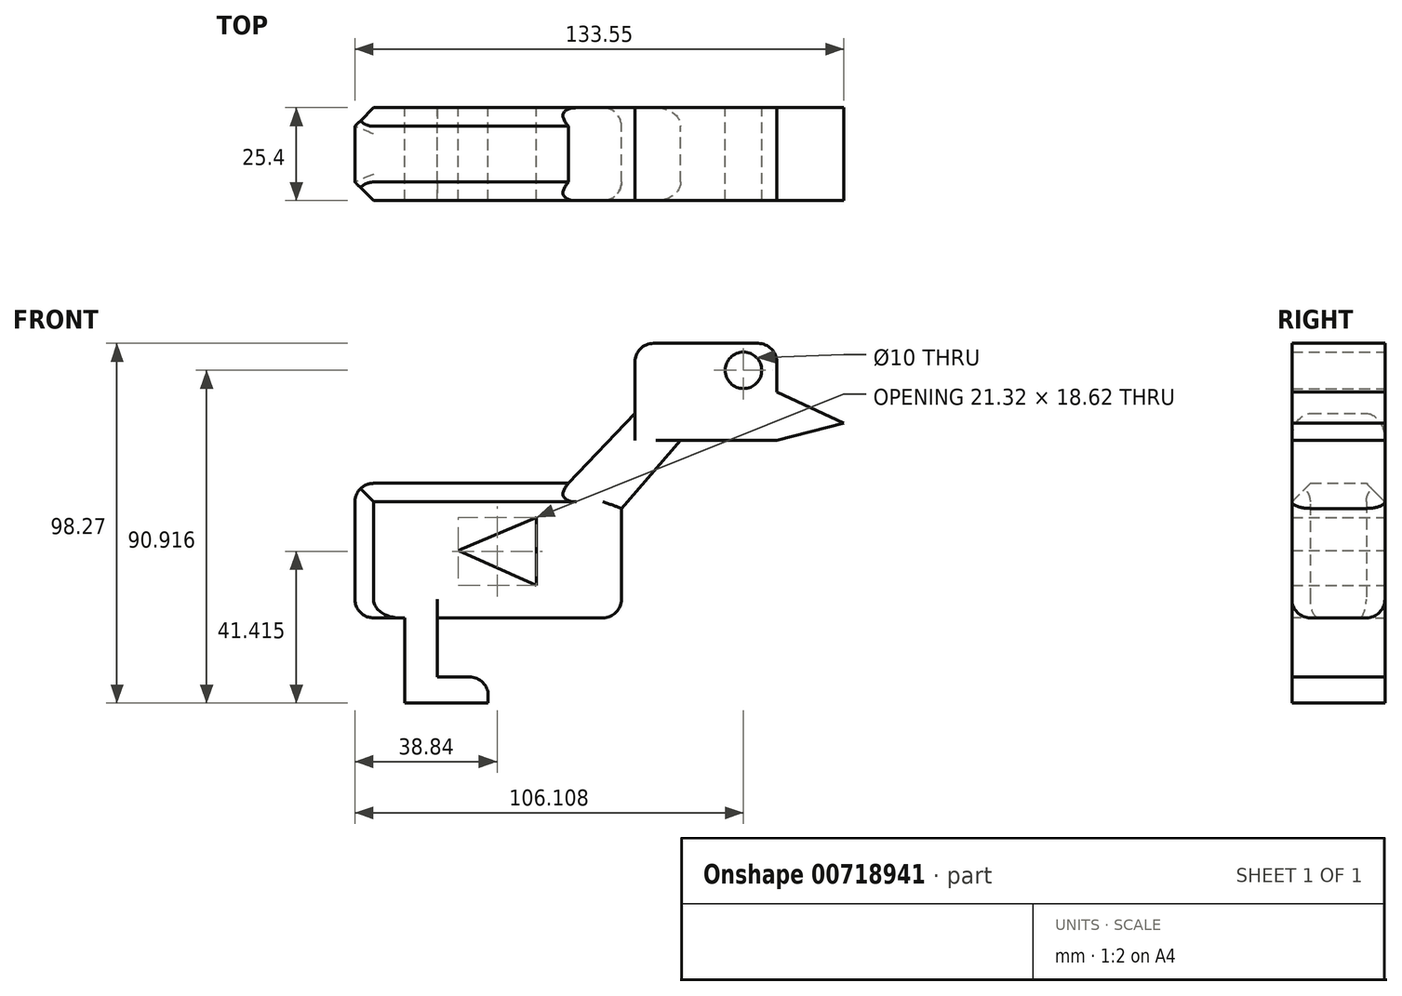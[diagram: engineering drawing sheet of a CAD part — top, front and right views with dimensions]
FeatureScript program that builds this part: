
annotation { "Feature Type Name" : "Feature", "Feature Type Description" : "" }
export const myFeature = defineFeature(function(context is Context, id is Id, definition is map)
    precondition{}
    {
        {
            var Q0;
            Q0=qCreatedBy(makeId("Front.planeOp"),FACE);
            var sketch = newSketch(context, id + "F0", { "sketchPlane" : qUnion([Q0])});
            skLineSegment(sketch, "E0.bottom", {"start": v(36.4, -18.38) * mm, "end": v(-13.9, -18.38) * mm});
            skLineSegment(sketch, "E0.top", {"start": v(36.4, 18.38) * mm, "end": v(-36.4, 18.38) * mm});
            skLineSegment(sketch, "E0.left", {"start": v(36.4, -18.38) * mm, "end": v(36.4, 18.38) * mm});
            skLineSegment(sketch, "E0.right", {"start": v(-36.4, -18.38) * mm, "end": v(-36.4, 18.38) * mm});
            skPoint(sketch, "E0.middle", {"position": v(0, 0) * mm});
            skLineSegment(sketch, "E1", {"start": v(21.93, 18.38) * mm, "end": v(40.56, 37.98) * mm});
            skLineSegment(sketch, "E2", {"start": v(36.4, 11.52) * mm, "end": v(52.56, 30.14) * mm});
            skLineSegment(sketch, "E3.bottom", {"start": v(78.78, 30.14) * mm, "end": v(52.56, 30.14) * mm});
            skLineSegment(sketch, "E3.top", {"start": v(78.78, 56.6) * mm, "end": v(40.07, 56.6) * mm});
            skLineSegment(sketch, "E3.left", {"start": v(78.78, 30.14) * mm, "end": v(78.78, 56.6) * mm});
            skLineSegment(sketch, "E3.right", {"start": v(40.07, 37.47) * mm, "end": v(40.07, 56.6) * mm});
            skPoint(sketch, "E3.middle", {"position": v(59.43, 43.37) * mm});
            skPoint(sketch, "E4.orphan", {"position": v(40.07, 30.14) * mm});
            skLineSegment(sketch, "E5", {"start": v(78.78, 43.37) * mm, "end": v(97.16, 34.8) * mm});
            skLineSegment(sketch, "E6", {"start": v(78.78, 30.14) * mm, "end": v(97.16, 34.8) * mm});
            skLineSegment(sketch, "E7", {"start": v(97.16, 34.8) * mm, "end": v(86.38, 34.8) * mm});
            skCircle(sketch, "E8", {"center": v(69.72, 49.26) * mm, "radius": 5 * mm});
            skLineSegment(sketch, "E9", {"start": v(13.11, 9.07) * mm, "end": v(13.11, -9.56) * mm});
            skLineSegment(sketch, "E10", {"start": v(13.11, -9.56) * mm, "end": v(-8.2, 0) * mm});
            skLineSegment(sketch, "E11", {"start": v(-8.2, 0) * mm, "end": v(13.11, 9.07) * mm});
            skLineSegment(sketch, "E12", {"start": v(-22.72, -18.38) * mm, "end": v(-22.72, -41.66) * mm});
            skLineSegment(sketch, "E13", {"start": v(-22.72, -41.66) * mm, "end": v(0, -41.66) * mm});
            skLineSegment(sketch, "E14", {"start": v(0, -41.66) * mm, "end": v(0, -34.55) * mm});
            skLineSegment(sketch, "E15", {"start": v(0, -34.55) * mm, "end": v(-13.9, -34.55) * mm});
            skLineSegment(sketch, "E16", {"start": v(-13.9, -34.55) * mm, "end": v(-13.9, -18.38) * mm});
            skLineSegment(sketch, "E17.trimOffspring", {"start": v(-22.72, -18.38) * mm, "end": v(-36.4, -18.38) * mm});
            skSolve(sketch);
        }
        {
            var Q0;
            {var subQ1=sQuery(id+"F0.wireOp",EDGE,"E0.bottom");Q0=makeQuery(id+"F0.imprint","IMPRINT",FACE,{"disambiguationData":[TD([[makeQuery(id+"F0.imprint","IMPRINT",EDGE,{"derivedFrom":subQ1}),-1.0]])]});}
            var Q1;
            {var subQ0=sQuery(id+"F0.wireOp",EDGE,"E2");Q1=makeQuery(id+"F0.imprint","IMPRINT",FACE,{"disambiguationData":[TD([[makeQuery(id+"F0.imprint","IMPRINT",EDGE,{"derivedFrom":subQ0}),1.0]])]});}
            var Q2;
            {var subQ2=sQuery(id+"F0.wireOp",EDGE,"E5");Q2=makeQuery(id+"F0.imprint","IMPRINT",FACE,{"disambiguationData":[TD([[makeQuery(id+"F0.imprint","IMPRINT",EDGE,{"derivedFrom":subQ2}),-1.0]])]});}
            extrude(context, id + "F1", {"entities" : qUnion([Q0, Q1, Q2]), "depth" : 25.4 * mm, "offsetDistance" : 25.4 * mm});
        }
        {
            var Q0;
            Q0=makeQuery(id+"F1.opExtrude","SWEPT_EDGE",EDGE,{"disambiguationData":[OSD([sQuery(id+"F0.wireOp",EDGE,"E14"),sQuery(id+"F0.wireOp",EDGE,"E15")])]});
            fillet(context, id + "F2", {"entities" : qUnion([Q0]), "radius" : 5.08 * mm, "tangentPropagation" : true, "allowEdgeOverflow" : false});
        }
        {
            var Q0;
            Q0=makeQuery(id+"F1.opExtrude","CAP_EDGE",EDGE,{"disambiguationData":[OSD([sQuery(id+"F0.wireOp",EDGE,"E0.top")])],"isStart":false});
            var Q1;
            Q1=makeQuery(id+"F1.opExtrude","CAP_EDGE",EDGE,{"disambiguationData":[OSD([sQuery(id+"F0.wireOp",EDGE,"E0.right")])],"isStart":false});
            chamfer(context, id + "F3", {"entities" : qUnion([Q0, Q1]), "width" : 5.08 * mm, "tangentPropagation" : true});
        }
        {
            var Q0;
            Q0=makeQuery(id+"F1.opExtrude","CAP_EDGE",EDGE,{"disambiguationData":[OSD([sQuery(id+"F0.wireOp",EDGE,"E0.top")])],"isStart":true});
            var Q1;
            Q1=makeQuery(id+"F1.opExtrude","CAP_EDGE",EDGE,{"disambiguationData":[OSD([sQuery(id+"F0.wireOp",EDGE,"E0.right")])],"isStart":true});
            chamfer(context, id + "F4", {"entities" : qUnion([Q0, Q1]), "width" : 5.08 * mm, "tangentPropagation" : true});
        }
        {
            var Q0;
            Q0=makeQuery(id+"F1.opExtrude","SWEPT_EDGE",EDGE,{"disambiguationData":[OSD([sQuery(id+"F0.wireOp",EDGE,"E0.top"),sQuery(id+"F0.wireOp",EDGE,"E0.right")])]});
            fillet(context, id + "F5", {"entities" : qUnion([Q0]), "radius" : 5.08 * mm, "tangentPropagation" : true, "allowEdgeOverflow" : false});
        }
        {
            var Q0;
            Q0=makeQuery(id+"F1.opExtrude","SWEPT_EDGE",EDGE,{"disambiguationData":[OSD([sQuery(id+"F0.wireOp",EDGE,"E3.top"),sQuery(id+"F0.wireOp",EDGE,"E3.left")])]});
            var Q1;
            Q1=makeQuery(id+"F1.opExtrude","SWEPT_EDGE",EDGE,{"disambiguationData":[OSD([sQuery(id+"F0.wireOp",EDGE,"E3.top"),sQuery(id+"F0.wireOp",EDGE,"E3.right")])]});
            fillet(context, id + "F6", {"entities" : qUnion([Q0, Q1]), "radius" : 5.08 * mm, "tangentPropagation" : true, "allowEdgeOverflow" : false});
        }
        {
            var Q0;
            Q0=makeQuery(id+"F1.opExtrude","SWEPT_EDGE",EDGE,{"disambiguationData":[OSD([sQuery(id+"F0.wireOp",EDGE,"E0.bottom"),sQuery(id+"F0.wireOp",EDGE,"E0.left")])]});
            fillet(context, id + "F7", {"entities" : qUnion([Q0]), "radius" : 5.08 * mm, "tangentPropagation" : true, "allowEdgeOverflow" : false});
        }
        {
            var Q0;
            Q0=makeQuery(id+"F1.opExtrude","SWEPT_EDGE",EDGE,{"disambiguationData":[OSD([sQuery(id+"F0.wireOp",EDGE,"E0.right"),sQuery(id+"F0.wireOp",EDGE,"E17.trimOffspring")])]});
            var Q1;
            Q1=makeQuery(id+"F3.opChamfer","BLEND_EDGE",EDGE,{"blendedFrom":[makeQuery(id+"F1.opExtrude","CAP_EDGE",EDGE,{"disambiguationData":[OSD([sQuery(id+"F0.wireOp",EDGE,"E0.right")])],"isStart":false}),makeQuery(id+"F1.opExtrude","SWEPT_FACE",FACE,{"disambiguationData":[OSD([sQuery(id+"F0.wireOp",EDGE,"E17.trimOffspring")])]})],"blendedInto":[makeQuery(id+"F1.opExtrude","SWEPT_FACE",FACE,{"disambiguationData":[OSD([sQuery(id+"F0.wireOp",EDGE,"E17.trimOffspring")])]})]});
            var Q2;
            Q2=makeQuery(id+"F4.opChamfer","BLEND_EDGE",EDGE,{"blendedFrom":[makeQuery(id+"F1.opExtrude","CAP_EDGE",EDGE,{"disambiguationData":[OSD([sQuery(id+"F0.wireOp",EDGE,"E0.right")])],"isStart":true}),makeQuery(id+"F1.opExtrude","SWEPT_FACE",FACE,{"disambiguationData":[OSD([sQuery(id+"F0.wireOp",EDGE,"E17.trimOffspring")])]})],"blendedInto":[makeQuery(id+"F1.opExtrude","SWEPT_FACE",FACE,{"disambiguationData":[OSD([sQuery(id+"F0.wireOp",EDGE,"E17.trimOffspring")])]})]});
            fillet(context, id + "F8", {"entities" : qUnion([Q0, Q1, Q2]), "radius" : 5.08 * mm, "tangentPropagation" : true, "allowEdgeOverflow" : false});
        }
        {
            var Q0;
            Q0=makeQuery(id+"F1.opExtrude","CAP_EDGE",EDGE,{"disambiguationData":[OSD([sQuery(id+"F0.wireOp",EDGE,"E1")])],"isStart":false});
            var Q1;
            Q1=makeQuery(id+"F1.opExtrude","CAP_EDGE",EDGE,{"disambiguationData":[OSD([sQuery(id+"F0.wireOp",EDGE,"E1")])],"isStart":true});
            var Q2;
            Q2=makeQuery(id+"F1.opExtrude","CAP_EDGE",EDGE,{"disambiguationData":[OSD([sQuery(id+"F0.wireOp",EDGE,"E2")])],"isStart":false});
            var Q3;
            Q3=makeQuery(id+"F1.opExtrude","CAP_EDGE",EDGE,{"disambiguationData":[OSD([sQuery(id+"F0.wireOp",EDGE,"E0.left")])],"isStart":false});
            var Q4;
            Q4=makeQuery(id+"F1.opExtrude","CAP_EDGE",EDGE,{"disambiguationData":[OSD([sQuery(id+"F0.wireOp",EDGE,"E2")])],"isStart":true});
            var Q5;
            Q5=makeQuery(id+"F1.opExtrude","CAP_EDGE",EDGE,{"disambiguationData":[OSD([sQuery(id+"F0.wireOp",EDGE,"E0.left")])],"isStart":true});
            fillet(context, id + "F9", {"entities" : qUnion([Q0, Q1, Q2, Q3, Q4, Q5]), "radius" : 5.08 * mm, "tangentPropagation" : true, "allowEdgeOverflow" : false});
        }
    });
